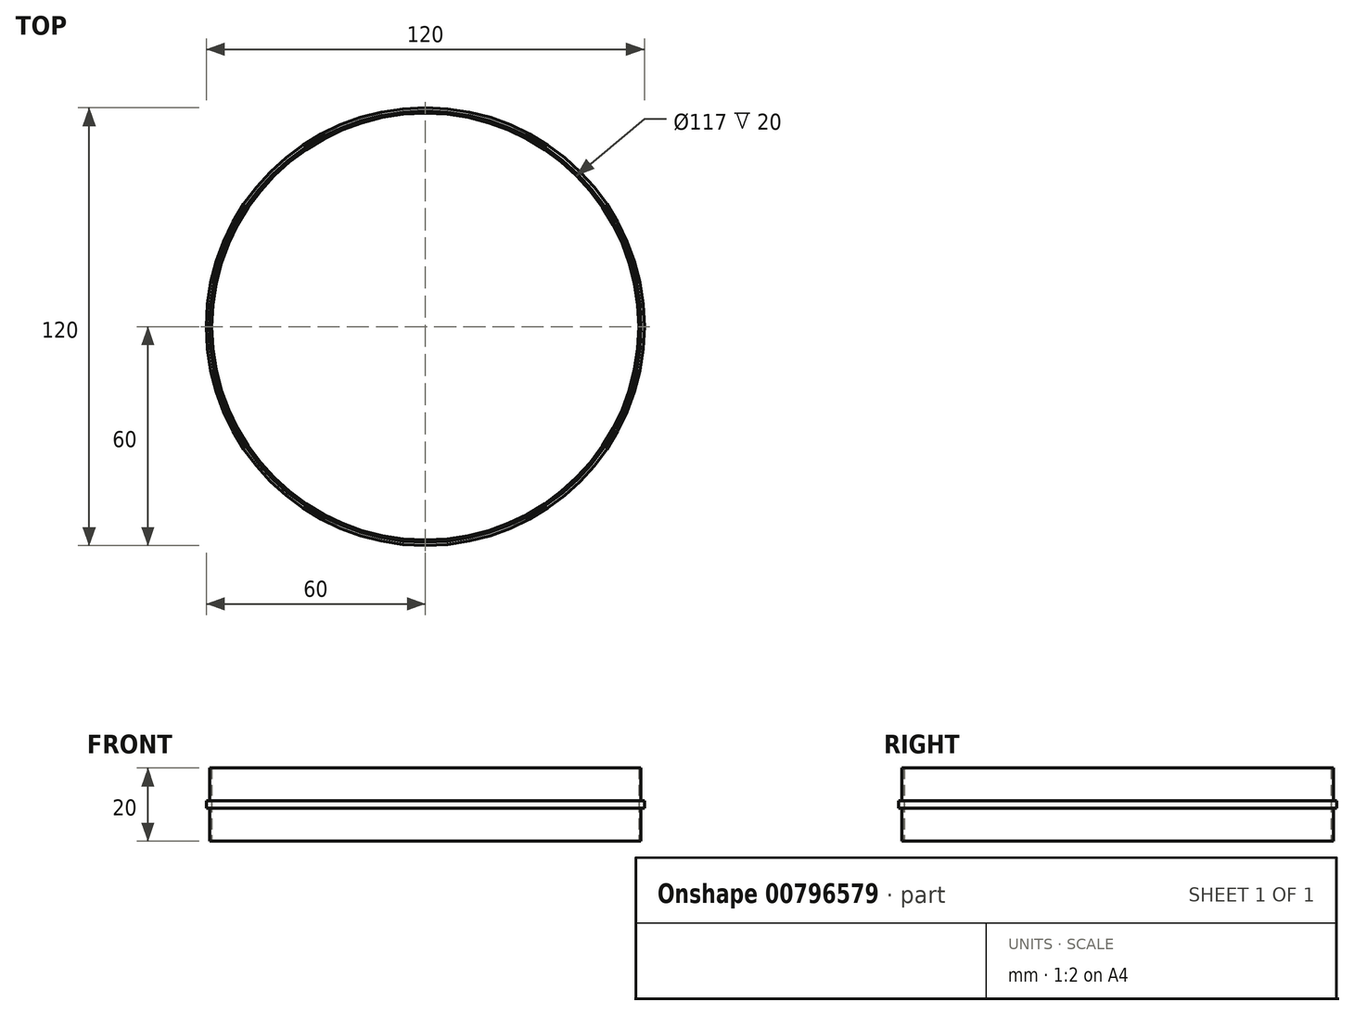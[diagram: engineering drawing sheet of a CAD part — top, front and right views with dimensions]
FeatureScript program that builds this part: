
annotation { "Feature Type Name" : "Feature", "Feature Type Description" : "" }
export const myFeature = defineFeature(function(context is Context, id is Id, definition is map)
    precondition{}
    {
        {
            var Q0;
            Q0=qCreatedBy(makeId("Top.planeOp"),FACE);
            var sketch = newSketch(context, id + "F0", { "sketchPlane" : qUnion([Q0])});
            skCircle(sketch, "E0", {"center": v(0, 0) * mm, "radius": 59.1 * mm});
            skCircle(sketch, "E1", {"center": v(0, 0) * mm, "radius": 58.5 * mm});
            skCircle(sketch, "E2", {"center": v(0, 0) * mm, "radius": 60 * mm});
            skSolve(sketch);
        }
        {
            var Q0;
            Q0=makeQuery(id+"F0.imprint","IMPRINT",FACE,{"disambiguationData":[TD([[makeQuery(id+"F0.imprint","IMPRINT",EDGE,{"derivedFrom":sQuery(id+"F0.wireOp",EDGE,"E0")}),1.0]])]});
            extrude(context, id + "F1", {"entities" : qUnion([Q0]), "depth" : 20 * mm, "offsetDistance" : 25 * mm});
        }
        {
            var Q0;
            Q0=makeQuery(id+"F0.imprint","IMPRINT",FACE,{"disambiguationData":[TD([[makeQuery(id+"F0.imprint","IMPRINT",EDGE,{"derivedFrom":sQuery(id+"F0.wireOp",EDGE,"E0")}),-1.0]])]});
            extrude(context, id + "F2", {"entities" : qUnion([Q0]), "operationType" : NewBodyOperationType.ADD, "depth" : 11 * mm, "offsetDistance" : 25 * mm, "hasSecondDirection" : true, "secondDirectionOppositeDirection" : false, "secondDirectionDepth" : 9 * mm});
        }
    });
